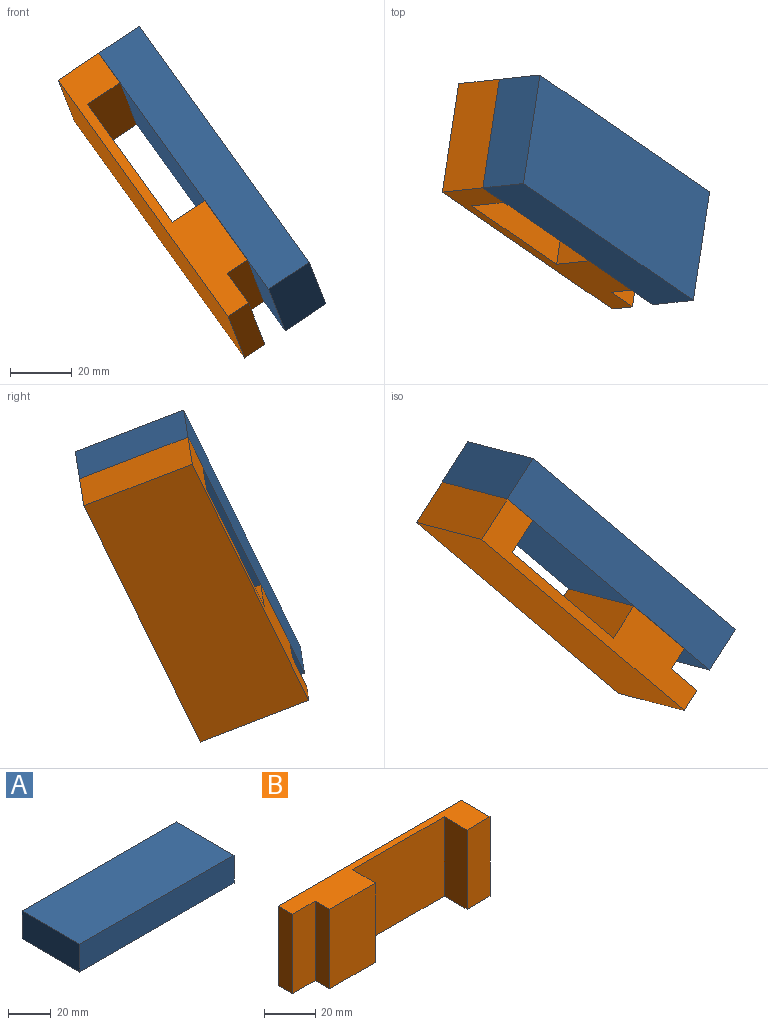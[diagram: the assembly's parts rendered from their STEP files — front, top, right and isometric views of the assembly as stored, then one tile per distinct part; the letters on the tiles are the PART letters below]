
ASSEMBLY  parts=2 mates=1
PART A: 6 faces, bbox 101.6x38.1x15.9 mm
  f0: plane 101.6x15.88mm, normal (0,-1,0), area 1612.9mm2, adj f1,f3,f4,f5
  f1: plane 38.1x15.88mm, normal (1,0,0), area 604.8mm2, adj f0,f2,f4,f5
  f2: plane 101.6x15.88mm, normal (0,1,0), area 1612.9mm2, adj f1,f3,f4,f5
  f3: plane 38.1x15.88mm, normal (-1,0,0), area 604.8mm2, adj f0,f2,f4,f5
  f4: plane 101.6x38.1mm, normal (0,0,-1), area 3871mm2, adj f0,f1,f2,f3
  f5: plane 101.6x38.1mm, normal (0,0,1), area 3871mm2, adj f0,f1,f2,f3
PART B: 12 faces, bbox 101.6x15.9x38.1 mm
  f0: plane 38.1x25.4mm, normal (0,-1,0), area 967.7mm2, adj f1,f9,f10,f11
  f1: plane 38.1x12.7mm, normal (1,0,0), area 483.9mm2, adj f0,f2,f10,f11
  f2: plane 50.8x38.1mm, normal (0,-1,0), area 1935.5mm2, adj f1,f3,f10,f11
  f3: plane 38.1x12.7mm, normal (-1,0,0), area 483.9mm2, adj f2,f4,f10,f11
  f4: plane 38.1x12.7mm, normal (0,-1,0), area 483.9mm2, adj f3,f5,f10,f11
  f5: plane 38.1x15.88mm, normal (1,0,0), area 604.8mm2, adj f4,f6,f10,f11
  f6: plane 101.6x38.1mm, normal (0,1,0), area 3871mm2, adj f5,f7,f10,f11
  f7: plane 38.1x7.94mm, normal (-1,0,0), area 302.4mm2, adj f6,f8,f10,f11
  f8: plane 38.1x12.7mm, normal (0,-1,0), area 483.9mm2, adj f7,f9,f10,f11
  f9: plane 38.1x7.94mm, normal (-1,0,0), area 302.4mm2, adj f0,f8,f10,f11
  f10: plane 101.6x15.88mm, normal (0,0,1), area 866.9mm2, adj f0,f1,f2,f3,f4,f5,f6,f7
  f11: plane 101.6x15.88mm, normal (0,0,-1), area 866.9mm2, adj f0,f1,f2,f3,f4,f5,f6,f7
PLACE A rot(axis=(0.88,-0.15,-0.46),165.4deg) t=(66.24,105.6,76.11)mm
PLACE B rot(axis=(0.24,-0.58,0.78),129.6deg) t=(96.44,104.34,31.06)mm
MATE ball B.f4 <-> A.f5  axis (0.83,0.09,0.55) through (38.7,124.48,114.4)mm
